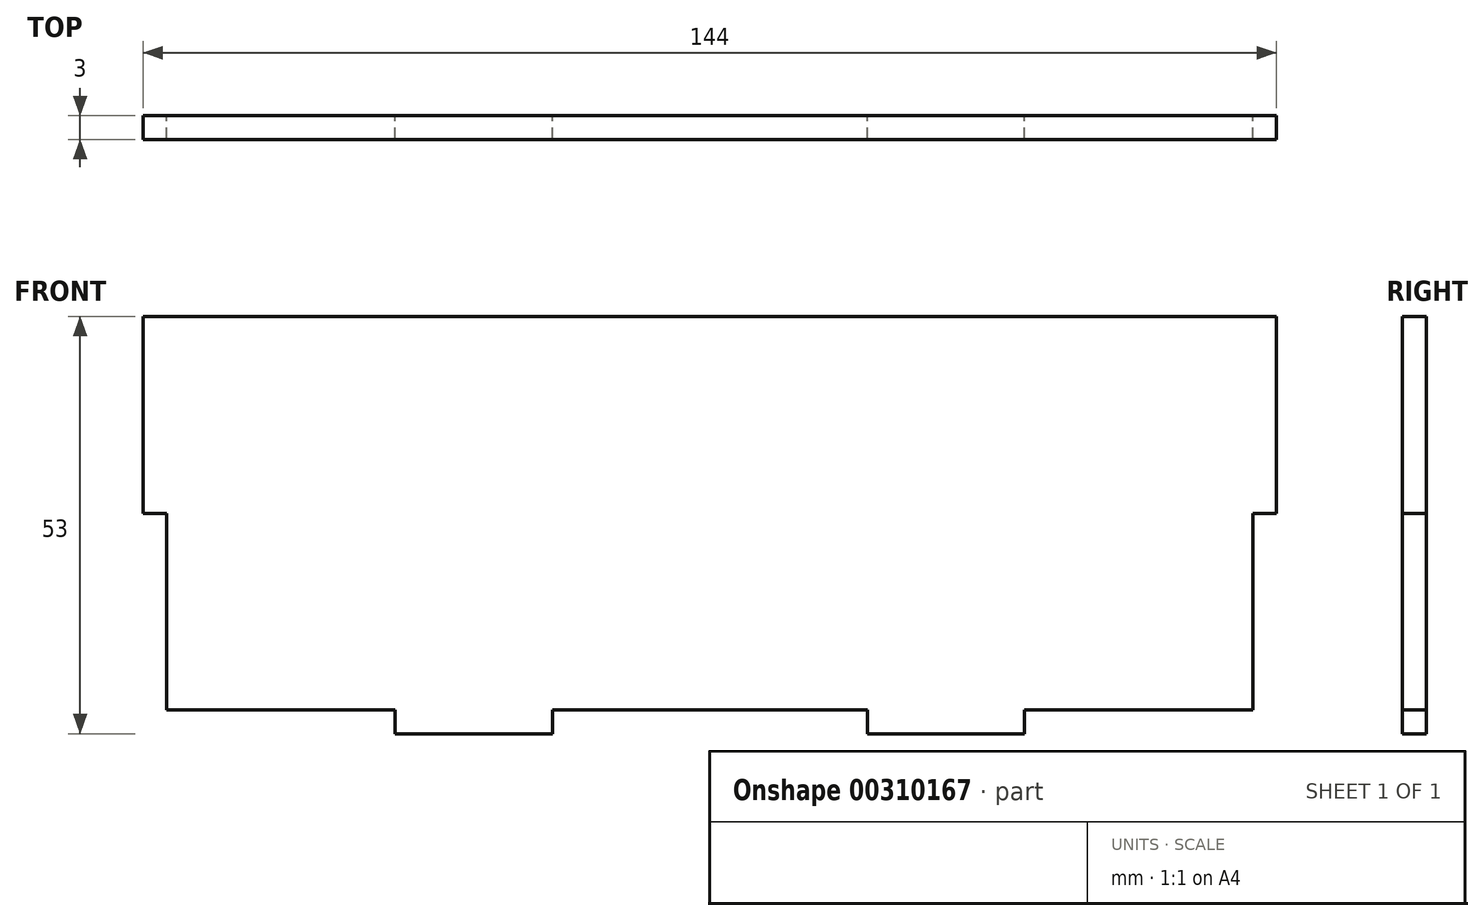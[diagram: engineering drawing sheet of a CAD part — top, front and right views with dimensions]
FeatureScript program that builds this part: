
annotation { "Feature Type Name" : "Feature", "Feature Type Description" : "" }
export const myFeature = defineFeature(function(context is Context, id is Id, definition is map)
    precondition{}
    {
        {
            var Q0;
            Q0=qCreatedBy(makeId("Front.planeOp"),FACE);
            var sketch = newSketch(context, id + "F0", { "sketchPlane" : qUnion([Q0])});
            skLineSegment(sketch, "E0.bottom", {"start": v(69, -25) * mm, "end": v(40, -25) * mm});
            skLineSegment(sketch, "E0.top", {"start": v(72, 25) * mm, "end": v(-72, 25) * mm});
            skLineSegment(sketch, "E0.left", {"start": v(72, 0) * mm, "end": v(72, 25) * mm});
            skLineSegment(sketch, "E0.right", {"start": v(-72, 0) * mm, "end": v(-72, 25) * mm});
            skPoint(sketch, "E0.middle", {"position": v(0, 0) * mm});
            skLineSegment(sketch, "E1.top", {"start": v(-20, -28) * mm, "end": v(-40, -28) * mm});
            skLineSegment(sketch, "E1.left", {"start": v(-20, -25) * mm, "end": v(-20, -28) * mm});
            skLineSegment(sketch, "E1.right", {"start": v(-40, -25) * mm, "end": v(-40, -28) * mm});
            skLineSegment(sketch, "E2.top", {"start": v(-72, 0) * mm, "end": v(-69, 0) * mm});
            skLineSegment(sketch, "E2.right", {"start": v(-69, -25) * mm, "end": v(-69, 0) * mm});
            skPoint(sketch, "E3.orphan", {"position": v(-72, -25) * mm});
            skLineSegment(sketch, "E4.trimOffspring", {"start": v(-40, -25) * mm, "end": v(-69, -25) * mm});
            skLineSegment(sketch, "E5.MirrorCS", {"start": v(69, -25) * mm, "end": v(69, 0) * mm});
            skLineSegment(sketch, "E6.MirrorCS", {"start": v(72, 0) * mm, "end": v(69, 0) * mm});
            skLineSegment(sketch, "E7.MirrorCS", {"start": v(20, -28) * mm, "end": v(40, -28) * mm});
            skLineSegment(sketch, "E8.MirrorCS", {"start": v(20, -25) * mm, "end": v(20, -28) * mm});
            skLineSegment(sketch, "E9.MirrorCS", {"start": v(40, -25) * mm, "end": v(40, -28) * mm});
            skLineSegment(sketch, "E10.trimOffspring", {"start": v(20, -25) * mm, "end": v(-20, -25) * mm});
            skPoint(sketch, "E11.orphan", {"position": v(72, -25) * mm});
            skSolve(sketch);
        }
        {
            var Q0;
            Q0 = qSketchRegion(id + "F0", true);
            extrude(context, id + "F1", {"entities" : qUnion([Q0]), "depth" : 3 * mm});
        }
    });
